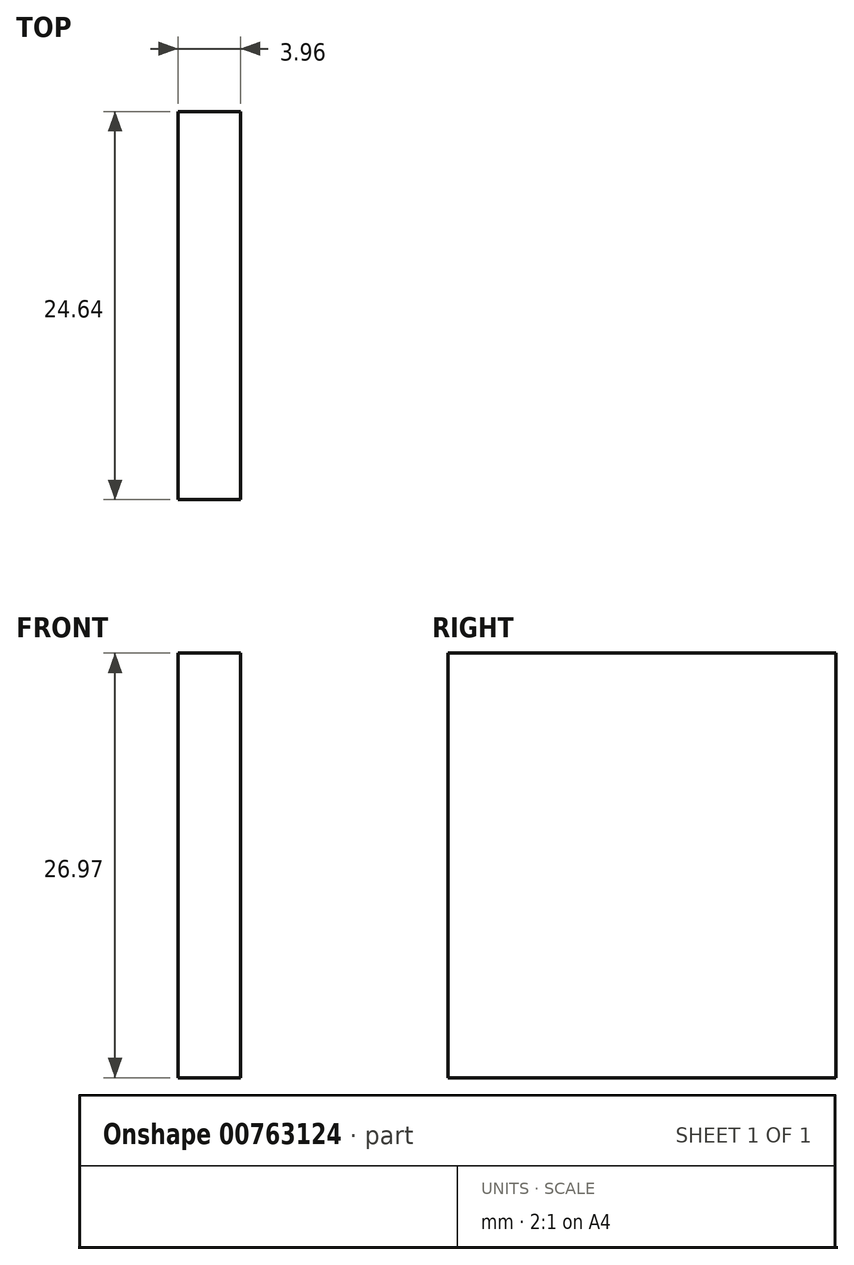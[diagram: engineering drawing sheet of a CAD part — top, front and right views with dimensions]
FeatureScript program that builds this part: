
annotation { "Feature Type Name" : "Feature", "Feature Type Description" : "" }
export const myFeature = defineFeature(function(context is Context, id is Id, definition is map)
    precondition{}
    {
        {
            var Q0;
            Q0=qCreatedBy(makeId("Front.planeOp"),FACE);
            var sketch = newSketch(context, id + "F0", { "sketchPlane" : qUnion([Q0])});
            skLineSegment(sketch, "E0.bottom", {"start": v(31.16, 26.97) * mm, "end": v(35.12, 26.97) * mm});
            skLineSegment(sketch, "E0.top", {"start": v(31.16, 0) * mm, "end": v(35.12, 0) * mm});
            skLineSegment(sketch, "E0.left", {"start": v(31.16, 26.97) * mm, "end": v(31.16, 0) * mm});
            skLineSegment(sketch, "E0.right", {"start": v(35.12, 26.97) * mm, "end": v(35.12, 0) * mm});
            skSolve(sketch);
        }
        {
            var Q0;
            Q0 = qSketchRegion(id + "F0", true);
            extrude(context, id + "F1", {"entities" : qUnion([Q0]), "depth" : 24.64 * mm, "offsetDistance" : 25.4 * mm});
        }
    });
